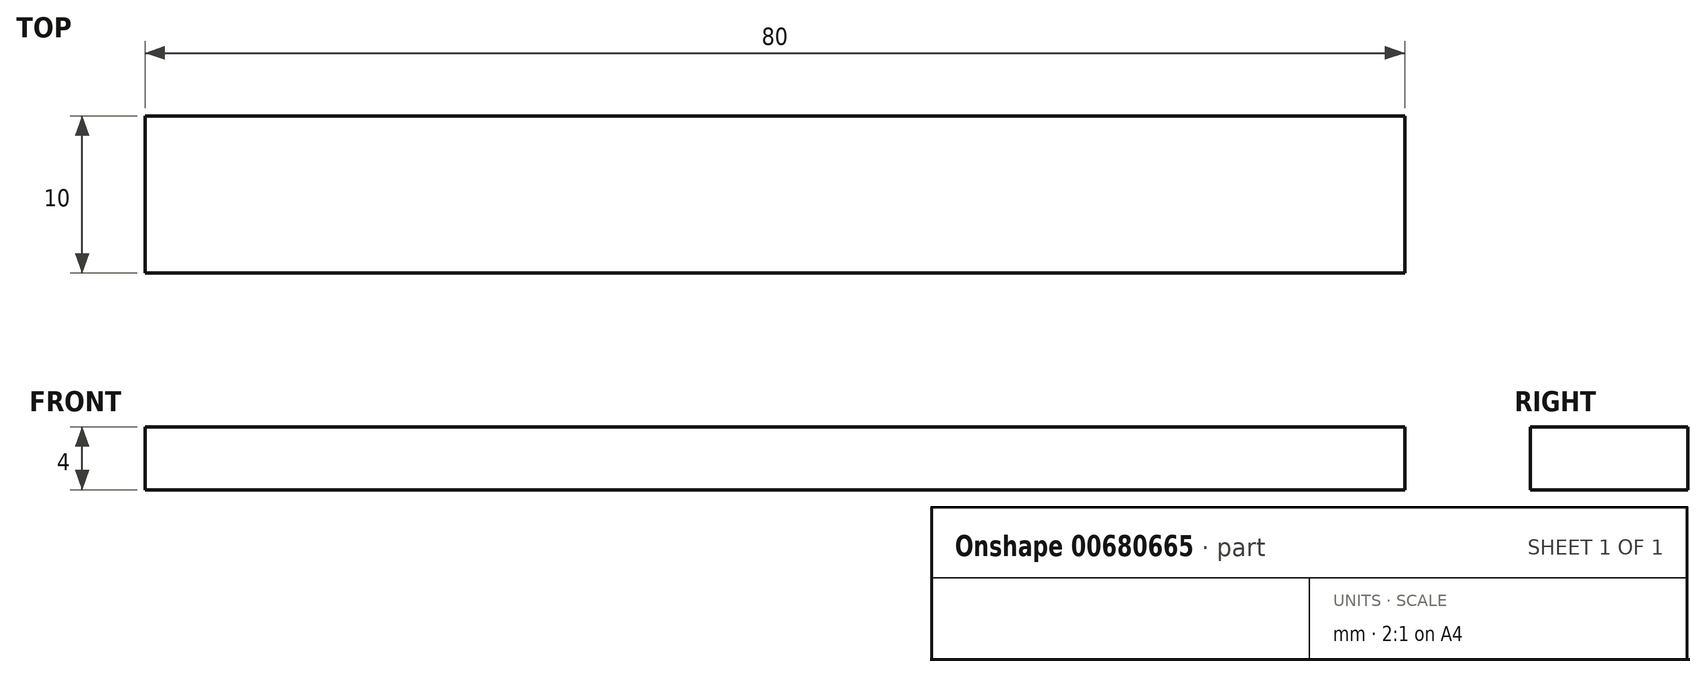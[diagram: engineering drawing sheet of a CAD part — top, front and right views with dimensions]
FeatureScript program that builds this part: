
annotation { "Feature Type Name" : "Feature", "Feature Type Description" : "" }
export const myFeature = defineFeature(function(context is Context, id is Id, definition is map)
    precondition{}
    {
        {
            var Q0;
            Q0=qCreatedBy(makeId("Top.planeOp"),FACE);
            var sketch = newSketch(context, id + "F0", { "sketchPlane" : qUnion([Q0])});
            skLineSegment(sketch, "E0", {"start": v(0, 0) * mm, "end": v(-80, 0) * mm});
            skLineSegment(sketch, "E1", {"start": v(-80, 0) * mm, "end": v(-80, 10) * mm});
            skLineSegment(sketch, "E2", {"start": v(-80, 10) * mm, "end": v(0, 10) * mm});
            skLineSegment(sketch, "E3", {"start": v(0, 10) * mm, "end": v(0, 0) * mm});
            skSolve(sketch);
        }
        {
            var Q0;
            Q0=makeQuery(id+"F0.imprint","IMPRINT",FACE,{"disambiguationData":[TD([[makeQuery(id+"F0.imprint","IMPRINT",EDGE,{"derivedFrom":sQuery(id+"F0.wireOp",EDGE,"E0")}),-1.0]])]});
            extrude(context, id + "F1", {"entities" : qUnion([Q0]), "depth" : 4 * mm, "offsetDistance" : 25 * mm});
        }
    });
